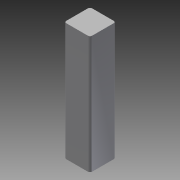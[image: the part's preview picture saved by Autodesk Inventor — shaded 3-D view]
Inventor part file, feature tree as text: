
AUTODESK INVENTOR PART (.ipt)
format: ipt  version: 2014 SP1 (Build 180222100, 222)  size: 81,408 bytes
history: native  units: in
note: dims shown in document units (in); Inventor stores cm internally (conversion verified against a paired STEP export)
features: extrude x1, fillet x1, sketch x1
ambient origin geometry x8: Origin, YZ Plane, XZ Plane, XY Plane, X Axis, Y Axis, Z Axis, Center Point
bodies: Solid1 (feature_tree)
feature tree (3):
  extrude  "Extrusion1"  Depth=0.125in
  fillet  "Fillet1"  Radius=0.57in
  sketch  "Sketch1"  dims[d0=0.125in d1=0.125in d2=0.57in d3=0.0in d4=0.01in]
